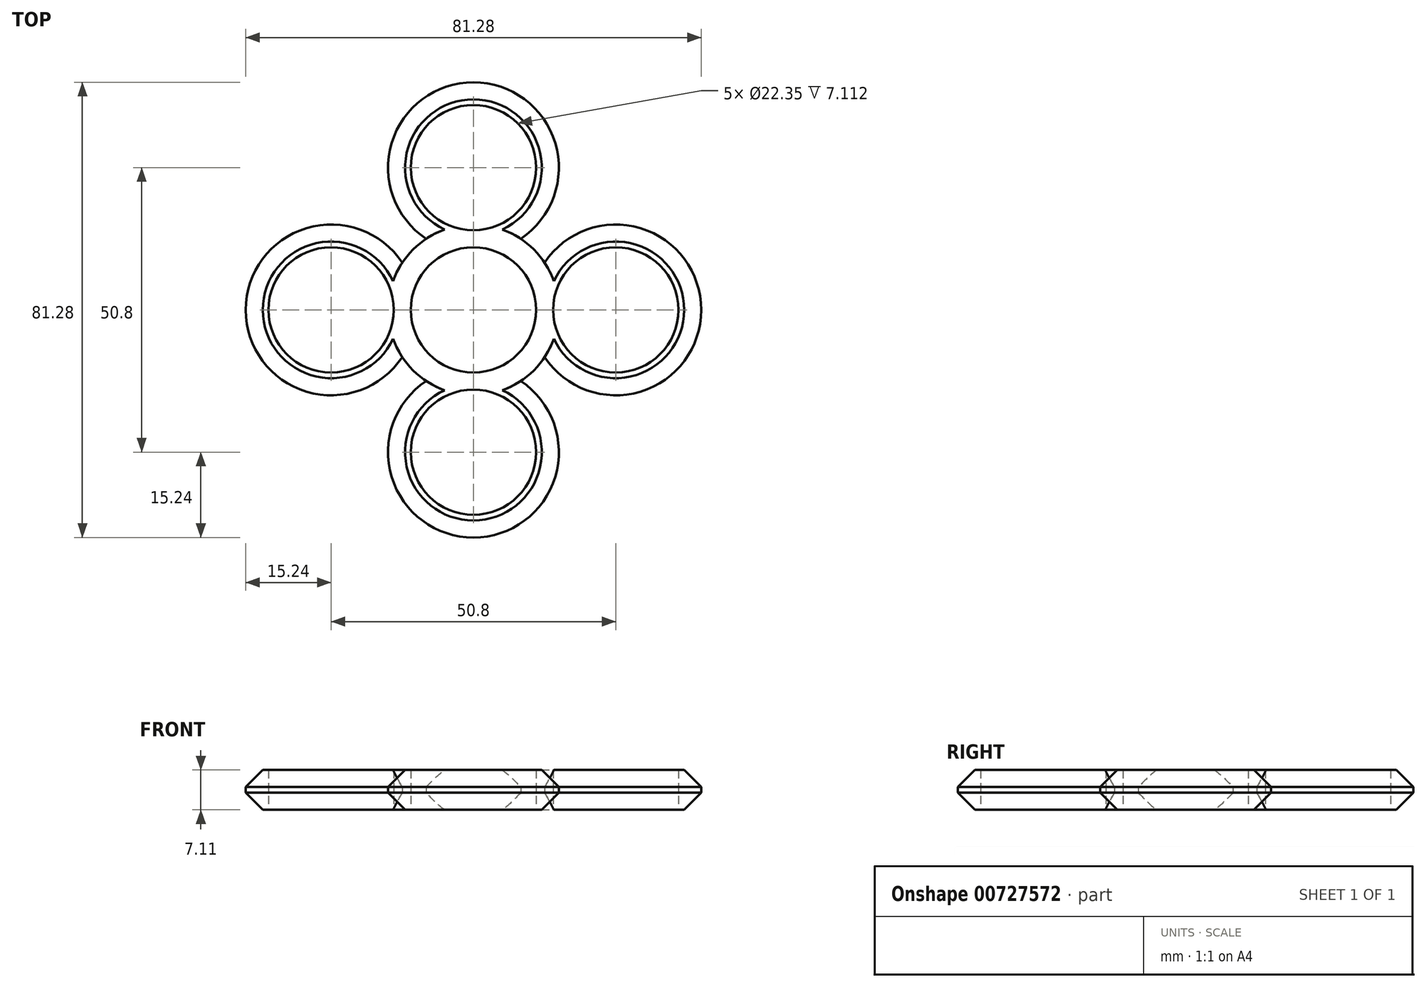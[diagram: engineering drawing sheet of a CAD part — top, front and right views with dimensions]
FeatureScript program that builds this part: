
annotation { "Feature Type Name" : "Feature", "Feature Type Description" : "" }
export const myFeature = defineFeature(function(context is Context, id is Id, definition is map)
    precondition{}
    {
        {
            var Q0;
            Q0=qCreatedBy(makeId("Top.planeOp"),FACE);
            var sketch = newSketch(context, id + "F0", { "sketchPlane" : qUnion([Q0])});
            skArc(sketch, "E0", {"start": v(-14.81, -3.58) * mm, "mid": v(-10.78, -10.78) * mm, "end": v(-3.58, -14.81) * mm});
            skCircle(sketch, "E1", {"center": v(0, 0) * mm, "radius": 11.18 * mm});
            skArc(sketch, "E2", {"start": v(8.42, 12.7) * mm, "mid": v(0, 40.64) * mm, "end": v(-8.42, 12.7) * mm});
            skArc(sketch, "E3", {"start": v(12.7, -8.42) * mm, "mid": v(40.64, 0) * mm, "end": v(12.7, 8.42) * mm});
            skArc(sketch, "E4", {"start": v(-8.42, -12.7) * mm, "mid": v(0, -40.64) * mm, "end": v(8.42, -12.7) * mm});
            skArc(sketch, "E5", {"start": v(-12.7, 8.42) * mm, "mid": v(-40.64, 0) * mm, "end": v(-12.7, -8.42) * mm});
            skPoint(sketch, "E6.orphan", {"position": v(-25.4, -15.24) * mm});
            skPoint(sketch, "E7.right.end.orphan", {"position": v(-25.4, 15.24) * mm});
            skPoint(sketch, "E8.orphan", {"position": v(-15.24, -25.4) * mm});
            skPoint(sketch, "E9.top.start.orphan", {"position": v(15.24, -25.4) * mm});
            skPoint(sketch, "E10.orphan", {"position": v(25.4, 15.24) * mm});
            skPoint(sketch, "E7.left.start.orphan", {"position": v(25.4, -15.24) * mm});
            skPoint(sketch, "E11.orphan", {"position": v(-15.24, 25.4) * mm});
            skPoint(sketch, "E9.bottom.start.orphan", {"position": v(15.24, 25.4) * mm});
            skCircle(sketch, "E12", {"center": v(-25.4, 0) * mm, "radius": 11.18 * mm});
            skCircle(sketch, "E13", {"center": v(0, 25.4) * mm, "radius": 11.18 * mm});
            skCircle(sketch, "E14", {"center": v(25.4, 0) * mm, "radius": 11.18 * mm});
            skCircle(sketch, "E15", {"center": v(0, -25.4) * mm, "radius": 11.18 * mm});
            skArc(sketch, "E16.trimOffspring", {"start": v(-3.58, 14.81) * mm, "mid": v(-10.78, 10.78) * mm, "end": v(-14.81, 3.58) * mm});
            skArc(sketch, "E17.trimOffspring", {"start": v(14.81, 3.58) * mm, "mid": v(10.78, 10.78) * mm, "end": v(3.58, 14.81) * mm});
            skArc(sketch, "E18.trimOffspring", {"start": v(3.58, -14.81) * mm, "mid": v(10.78, -10.78) * mm, "end": v(14.81, -3.58) * mm});
            skSolve(sketch);
        }
        {
            var Q0;
            Q0 = qSketchRegion(id + "F0", true);
            extrude(context, id + "F1", {"entities" : qUnion([Q0]), "depth" : 7.11 * mm, "offsetDistance" : 25.4 * mm});
        }
        {
            var Q0;
            Q0=makeQuery(id+"F1.opExtrude","CAP_EDGE",EDGE,{"disambiguationData":[OSD([sQuery(id+"F0.wireOp",EDGE,"E2")])],"isStart":false});
            var Q1;
            Q1=makeQuery(id+"F1.opExtrude","CAP_EDGE",EDGE,{"disambiguationData":[OSD([sQuery(id+"F0.wireOp",EDGE,"E2")])],"isStart":true});
            var Q2;
            Q2=makeQuery(id+"F1.opExtrude","CAP_EDGE",EDGE,{"disambiguationData":[OSD([sQuery(id+"F0.wireOp",EDGE,"E3")])],"isStart":false});
            var Q3;
            Q3=makeQuery(id+"F1.opExtrude","CAP_EDGE",EDGE,{"disambiguationData":[OSD([sQuery(id+"F0.wireOp",EDGE,"E3")])],"isStart":true});
            var Q4;
            Q4=makeQuery(id+"F1.opExtrude","CAP_EDGE",EDGE,{"disambiguationData":[OSD([sQuery(id+"F0.wireOp",EDGE,"E4")])],"isStart":false});
            var Q5;
            Q5=makeQuery(id+"F1.opExtrude","CAP_EDGE",EDGE,{"disambiguationData":[OSD([sQuery(id+"F0.wireOp",EDGE,"E4")])],"isStart":true});
            var Q6;
            Q6=makeQuery(id+"F1.opExtrude","CAP_EDGE",EDGE,{"disambiguationData":[OSD([sQuery(id+"F0.wireOp",EDGE,"E5")])],"isStart":false});
            var Q7;
            Q7=makeQuery(id+"F1.opExtrude","CAP_EDGE",EDGE,{"disambiguationData":[OSD([sQuery(id+"F0.wireOp",EDGE,"E5")])],"isStart":true});
            chamfer(context, id + "F2", {"entities" : qUnion([Q0, Q1, Q2, Q3, Q4, Q5, Q6, Q7]), "width" : 3.05 * mm, "tangentPropagation" : true});
        }
    });
